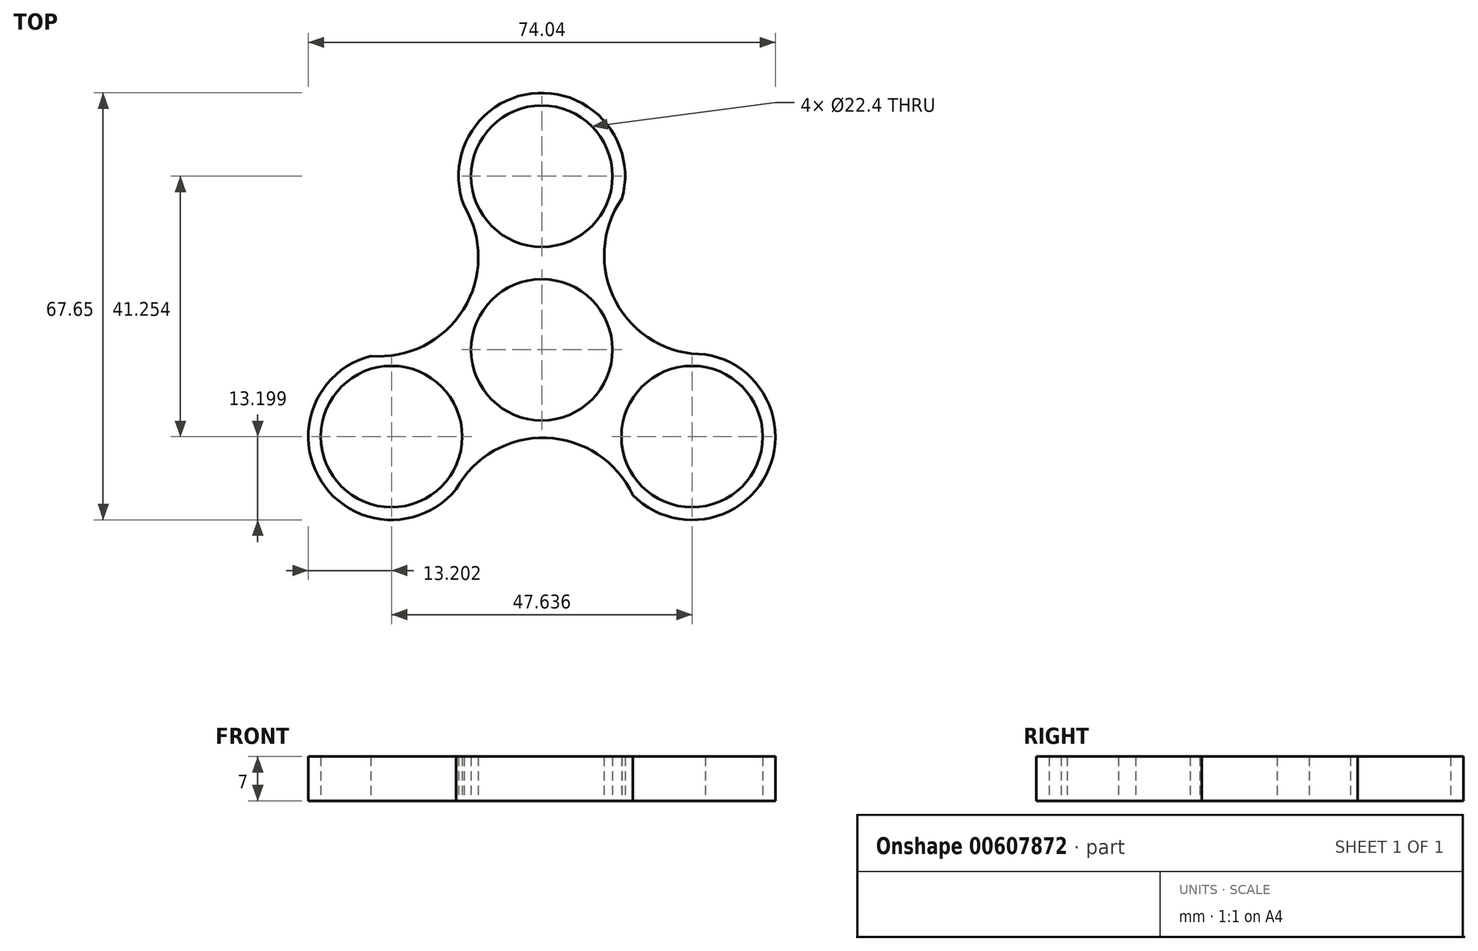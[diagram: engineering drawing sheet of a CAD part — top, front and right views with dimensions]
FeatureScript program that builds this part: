
annotation { "Feature Type Name" : "Feature", "Feature Type Description" : "" }
export const myFeature = defineFeature(function(context is Context, id is Id, definition is map)
    precondition{}
    {
        {
            var Q0;
            Q0=qCreatedBy(makeId("Top.planeOp"),FACE);
            var sketch = newSketch(context, id + "F0", { "sketchPlane" : qUnion([Q0])});
            skCircle(sketch, "E0", {"center": v(0, 0) * mm, "radius": 11.2 * mm});
            skCircle(sketch, "E1", {"center": v(0, 27.5) * mm, "radius": 11.2 * mm});
            skArc(sketch, "E2", {"start": v(10.58, 19.61) * mm, "mid": v(0.53, 40.7) * mm, "end": v(-11.18, 20.48) * mm});
            skArc(sketch, "E3.1.0", {"start": v(-22.28, -0.64) * mm, "mid": v(-35.5, -19.9) * mm, "end": v(-12.15, -19.92) * mm});
            skCircle(sketch, "E3.1.1", {"center": v(-23.82, -13.75) * mm, "radius": 11.2 * mm});
            skArc(sketch, "E3.2.0", {"start": v(11.7, -18.97) * mm, "mid": v(34.98, -20.8) * mm, "end": v(23.33, -0.56) * mm});
            skCircle(sketch, "E3.2.1", {"center": v(23.82, -13.75) * mm, "radius": 11.2 * mm});
            skArc(sketch, "E4", {"start": v(12.72, 23.97) * mm, "mid": v(11.73, 7.58) * mm, "end": v(25.91, -0.72) * mm});
            skArc(sketch, "E5.1.0", {"start": v(-27.12, -0.97) * mm, "mid": v(-12.43, 6.37) * mm, "end": v(-12.33, 22.8) * mm});
            skArc(sketch, "E5.2.0", {"start": v(14.4, -23) * mm, "mid": v(0.7, -13.95) * mm, "end": v(-13.58, -22.08) * mm});
            skSolve(sketch);
        }
        {
            var Q0;
            Q0=makeQuery(id+"F0.imprint","IMPRINT",FACE,{"disambiguationData":[TD([[makeQuery(id+"F0.imprint","IMPRINT",EDGE,{"derivedFrom":sQuery(id+"F0.wireOp",EDGE,"E0")}),-1.0]])]});
            extrude(context, id + "F1", {"entities" : qUnion([Q0]), "depth" : 7 * mm, "offsetDistance" : 25 * mm});
        }
    });
